# Revit family: Shower-Rainhead-KOHLER-Open_Rain-26301W_1
name_source: partatom
category: Plumbing Fixtures
revit_build: Autodesk Revit 2017 (Build: 20160225_1515(x64)
units: mm (PartAtom-declared; Revit-internal decimal feet)

## family parameters
Cut with Voids When Loaded = No
Host = Face
OmniClass Number = 23.31.17.00
OmniClass Title = Showers
Part Type = Normal
Room Calculation Point = No
Round Connector Dimension = Use Diameter
Shared = No

## types (2) — shared parameters
ADA Compliant = No
Assembly Code = D2010700
CW Connection = No
Cold Water Inlet = Cold Water Inlet
Date Modified = 03/09/2021
Default Elevation = 42"
Drain Included = No
Finish = Kohler-Metal-CP-Polished_Chrome
HW Connection = Yes
Height = 8 7/8"
Hot Water Inlet = Hot Water Inlet
Length = 5 1/4"
Manufacturer = KOHLER Co.
Master Format 2014 = 22 42 23
Master Format 2014 Name = Residential Showers
Material = Premium Metal Construction
Panel Thickness = 13/16"
Pressure = 80.00 psi
Product Name = Open Rain
Tempered Water Inlet = Tempered Water Inlet
URL = https://www.kohler.co.uk
Vent Connection = No
Waste Connection = No
Waste Water Outlet = Waste Water Outlet
WaterSense Certified = No
Width = 8 7/8"

## per-type parameters (varying)
| type | Description | Flow Rate | Model | Type |
| 2.5 GPM, CP-Polished Chrome | OPEN RAIN RAINHEAD, 2.5GPM | 3 GPM | 26301W-CP | 1 |
| 1.75 GPM, CP-Polished Chrome | OPEN RAIN RAINHEAD, 1.75GPM | 2 GPM | 26301W-G-CP | 2 |

## geometry (parser evidence)
native form markers: Sweep x5
no freeform markers — native parametric forms only
